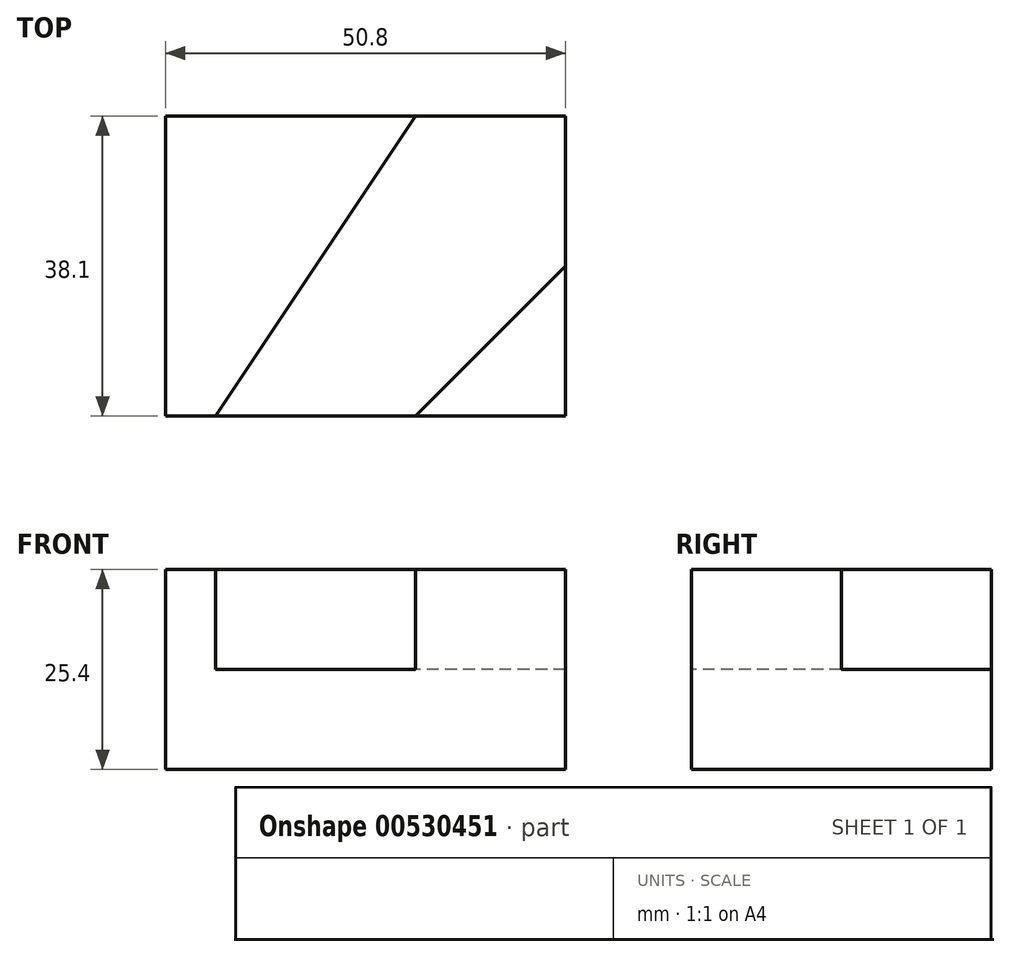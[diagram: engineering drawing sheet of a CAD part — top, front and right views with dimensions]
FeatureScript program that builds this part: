
annotation { "Feature Type Name" : "Feature", "Feature Type Description" : "" }
export const myFeature = defineFeature(function(context is Context, id is Id, definition is map)
    precondition{}
    {
        {
            var Q0;
            Q0=qCreatedBy(makeId("Top.planeOp"),FACE);
            var sketch = newSketch(context, id + "F0", { "sketchPlane" : qUnion([Q0])});
            skLineSegment(sketch, "E0", {"start": v(-71.5, 63.56) * mm, "end": v(-71.5, 25.46) * mm});
            skLineSegment(sketch, "E1", {"start": v(-71.5, 25.46) * mm, "end": v(-20.7, 25.46) * mm});
            skLineSegment(sketch, "E2", {"start": v(-20.7, 25.46) * mm, "end": v(-20.7, 63.56) * mm});
            skLineSegment(sketch, "E3", {"start": v(-20.7, 63.56) * mm, "end": v(-71.5, 63.56) * mm});
            skSolve(sketch);
        }
        {
            var Q0;
            Q0=makeQuery(id+"F0.imprint","IMPRINT",FACE,{"disambiguationData":[TD([[makeQuery(id+"F0.imprint","IMPRINT",EDGE,{"derivedFrom":sQuery(id+"F0.wireOp",EDGE,"E0")}),1.0]])]});
            extrude(context, id + "F1", {"entities" : qUnion([Q0]), "depth" : 25.4 * mm, "offsetDistance" : 25.4 * mm});
        }
        {
            var Q0;
            Q0=makeQuery(id+"F1.opExtrude","CAP_FACE",FACE,{"disambiguationData":[OSD([sQuery(id+"F0.wireOp",EDGE,"E0"),sQuery(id+"F0.wireOp",EDGE,"E1"),sQuery(id+"F0.wireOp",EDGE,"E2"),sQuery(id+"F0.wireOp",EDGE,"E3")])],"isStart":false});
            var sketch = newSketch(context, id + "F2", { "sketchPlane" : qUnion([Q0])});
            skLineSegment(sketch, "E4", {"start": v(-39.75, 63.56) * mm, "end": v(-65.15, 25.46) * mm});
            skLineSegment(sketch, "E5", {"start": v(-65.15, 25.46) * mm, "end": v(-39.75, 25.46) * mm});
            skLineSegment(sketch, "E6", {"start": v(-39.75, 25.46) * mm, "end": v(-20.7, 44.51) * mm});
            skLineSegment(sketch, "E7", {"start": v(-20.7, 44.51) * mm, "end": v(-20.7, 63.56) * mm});
            skLineSegment(sketch, "E8", {"start": v(-20.7, 63.56) * mm, "end": v(-39.75, 63.56) * mm});
            skSolve(sketch);
        }
        {
            var Q0;
            Q0=makeQuery(id+"F2.imprint","IMPRINT",FACE,{"disambiguationData":[TD([[makeQuery(id+"F2.imprint","IMPRINT",EDGE,{"derivedFrom":sQuery(id+"F2.wireOp",EDGE,"E4")}),1.0]])]});
            extrude(context, id + "F3", {"entities" : qUnion([Q0]), "operationType" : NewBodyOperationType.REMOVE, "oppositeDirection" : true, "depth" : 12.7 * mm, "offsetDistance" : 25.4 * mm});
        }
    });
